# Revit family: Zumtobel TECTON MIREL LED
name_source: partatom
category: Lighting Fixtures
revit_build: Autodesk Revit 2016 (Build: 20150220_1215(x64)
units: mm (PartAtom-declared; Revit-internal decimal feet)

## family parameters
Cut with Voids When Loaded = No
Host = Face
Light Source = No
OmniClass Number = 23.80.70.11
OmniClass Title = Luminaries for Internal Lighting
Part Type = Normal
Room Calculation Point = No
Round Connector Dimension = Use Diameter
Shared = No

## types (6) — shared parameters
Apparent Load = 0 VA
Assembly Code = D5020210
Description = LED continuous-row luminaire
Manufacturer = Zumtobel Lighting
URL = http://www.zumtobel.com
zero-valued in all types: Default Elevation, Offset

## per-type parameters (varying)
| type | Fixture Type | Length |
| TECTON MIREL LED3700 L1000 | Zumtobel TECTON MIREL LED (Lamp & Reflector) : TECTON MIREL LED3700 L1000 | 1000 mm  [stored 3.28084 ft] |
| TECTON MIREL LED5500 L1500 | Zumtobel TECTON MIREL LED (Lamp & Reflector) : TECTON MIREL LED5500 L1500 | 1500 mm  [stored 4.92126 ft] |
| TECTON MIREL LED7400 L2000 | Zumtobel TECTON MIREL LED (Lamp & Reflector) : TECTON MIREL LED7400 L2000 | 2000 mm  [stored 6.56168 ft] |
| TECTON MIREL LED2700 L1000 | Zumtobel TECTON MIREL LED (Lamp & Reflector) : TECTON MIREL LED2700 L1000 | 1000 mm  [stored 3.28084 ft] |
| TECTON MIREL LED4000 L1500 | Zumtobel TECTON MIREL LED (Lamp & Reflector) : TECTON MIREL LED4000 L1500 | 1500 mm  [stored 4.92126 ft] |
| TECTON MIREL LED5400 L2000 | Zumtobel TECTON MIREL LED (Lamp & Reflector) : TECTON MIREL LED5400 L2000 | 2000 mm  [stored 6.56168 ft] |

note: [stored X ft] marks values corroborated as IEEE doubles in the binary element streams (Revit-internal decimal feet)

## geometry (parser evidence)
native form markers: Blend x18, Sweep x17
no freeform markers — native parametric forms only
